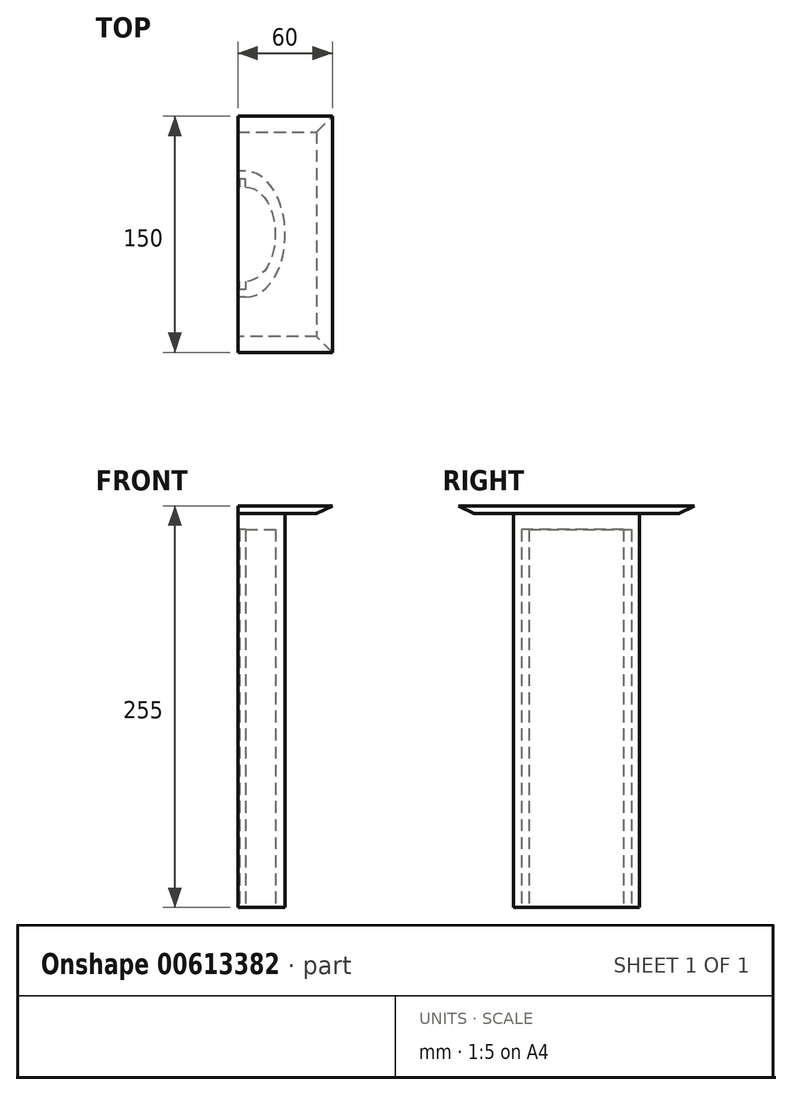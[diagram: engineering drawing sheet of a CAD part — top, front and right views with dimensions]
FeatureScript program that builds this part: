
annotation { "Feature Type Name" : "Feature", "Feature Type Description" : "" }
export const myFeature = defineFeature(function(context is Context, id is Id, definition is map)
    precondition{}
    {
        {
            var Q0;
            Q0=qCreatedBy(makeId("Top.planeOp"),FACE);
            var sketch = newSketch(context, id + "F0", { "sketchPlane" : qUnion([Q0])});
            skEllipticalArc(sketch, "E0", {});
            skPoint(sketch, "E1.oppositeSnap0", {"position": v(6, 33.86) * mm});
            skLineSegment(sketch, "E1.bottom", {"start": v(6, -46.14) * mm, "end": v(1, -46.14) * mm});
            skLineSegment(sketch, "E1.top", {"start": v(6, 33.86) * mm, "end": v(1, 33.86) * mm});
            skLineSegment(sketch, "E1.right", {"start": v(1, -46.14) * mm, "end": v(1, 33.86) * mm});
            const initialGuessF0  = {"E0": [0.006, -0.006144226491451254, 0, -1, 0.04, 0.025, 0, 3.141592653589793]};
            skSetInitialGuess(sketch, initialGuessF0);
            skSolve(sketch);
        }
        {
            var Q0;
            Q0=makeQuery(id+"F0.imprint","IMPRINT",FACE,{"disambiguationData":[TD([[makeQuery(id+"F0.imprint","IMPRINT",EDGE,{"derivedFrom":sQuery(id+"F0.wireOp",EDGE,"E0")}),1.0]])]});
            extrude(context, id + "F1", {"entities" : qUnion([Q0]), "depth" : 250 * mm, "offsetDistance" : 25 * mm});
        }
        {
            var Q0;
            Q0=makeQuery(id+"F1.opExtrude","CAP_FACE",FACE,{"disambiguationData":[OSD([sQuery(id+"F0.wireOp",EDGE,"E0"),sQuery(id+"F0.wireOp",EDGE,"E1.bottom"),sQuery(id+"F0.wireOp",EDGE,"E1.top"),sQuery(id+"F0.wireOp",EDGE,"E1.right")])],"isStart":false});
            var sketch = newSketch(context, id + "F2", { "sketchPlane" : qUnion([Q0])});
            skLineSegment(sketch, "E2.bottom", {"start": v(61, 68.86) * mm, "end": v(1, 68.86) * mm});
            skLineSegment(sketch, "E2.top", {"start": v(61, -81.14) * mm, "end": v(1, -81.14) * mm});
            skLineSegment(sketch, "E2.left", {"start": v(61, 68.86) * mm, "end": v(61, -81.14) * mm});
            skLineSegment(sketch, "E2.right", {"start": v(1, 68.86) * mm, "end": v(1, -81.14) * mm});
            skSolve(sketch);
        }
        {
            var Q0;
            {var subQ2=sQuery(id+"F2.wireOp",EDGE,"E2.bottom");Q0=makeQuery(id+"F2.imprint","IMPRINT",FACE,{"disambiguationData":[TD([[makeQuery(id+"F2.imprint","IMPRINT",EDGE,{"derivedFrom":subQ2}),1.0]])]});}
            var Q1;
            Q1=makeQuery(id+"F2.imprint","IMPRINT",FACE,{"disambiguationData":[TD([[makeQuery(id+"F2.imprint","IMPRINT",EDGE,{"derivedFrom":makeQuery(id+"F1.opExtrude","CAP_EDGE",EDGE,{"disambiguationData":[OSD([sQuery(id+"F0.wireOp",EDGE,"E0")])],"isStart":false})}),1.0]])]});
            extrude(context, id + "F3", {"entities" : qUnion([Q0, Q1]), "operationType" : NewBodyOperationType.ADD, "depth" : 5 * mm, "offsetDistance" : 25 * mm});
        }
        {
            var Q0;
            Q0=makeQuery(id+"F3.opExtrude","CAP_EDGE",EDGE,{"disambiguationData":[OSD([sQuery(id+"F2.wireOp",EDGE,"E2.bottom")])],"isStart":true});
            var Q1;
            Q1=makeQuery(id+"F3.opExtrude","CAP_EDGE",EDGE,{"disambiguationData":[OSD([sQuery(id+"F2.wireOp",EDGE,"E2.left")])],"isStart":true});
            var Q2;
            Q2=makeQuery(id+"F3.opExtrude","CAP_EDGE",EDGE,{"disambiguationData":[OSD([sQuery(id+"F2.wireOp",EDGE,"E2.top")])],"isStart":true});
            chamfer(context, id + "F4", {"entities" : qUnion([Q0, Q1, Q2]), "chamferType" : ChamferType.TWO_OFFSETS, "width1" : 5 * mm, "oppositeDirection" : false, "width2" : 10 * mm, "tangentPropagation" : true});
        }
        {
            var Q0;
            Q0=makeQuery(id+"F1.opExtrude","CAP_FACE",FACE,{"disambiguationData":[OSD([sQuery(id+"F0.wireOp",EDGE,"E0"),sQuery(id+"F0.wireOp",EDGE,"E1.bottom"),sQuery(id+"F0.wireOp",EDGE,"E1.top"),sQuery(id+"F0.wireOp",EDGE,"E1.right")])],"isStart":true});
            var sketch = newSketch(context, id + "F5", { "sketchPlane" : qUnion([Q0])});
            skEllipticalArc(sketch, "E3", {});
            skLineSegment(sketch, "E4", {"start": v(6, -23.86) * mm, "end": v(1, -23.86) * mm});
            skLineSegment(sketch, "E5", {"start": v(6, 36.14) * mm, "end": v(1, 36.14) * mm});
            skLineSegment(sketch, "E6", {"start": v(1, -23.86) * mm, "end": v(1, 36.14) * mm});
            skPoint(sketch, "E7.orphan", {"position": v(0, -23.86) * mm});
            skLineSegment(sketch, "E8.bottom", {"start": v(3.5, -23.86) * mm, "end": v(6, -23.86) * mm});
            skLineSegment(sketch, "E8.right", {"start": v(6, -23.86) * mm, "end": v(6, -28.86) * mm});
            skLineSegment(sketch, "E9", {"start": v(1, 6.14) * mm, "end": v(6, 6.14) * mm});
            skPoint(sketch, "E8.top.start.orphan", {"position": v(3.5, -28.86) * mm});
            skLineSegment(sketch, "E10", {"start": v(6, -28.86) * mm, "end": v(2, -28.86) * mm});
            skLineSegment(sketch, "E11", {"start": v(2, -28.86) * mm, "end": v(2, -23.86) * mm});
            skLineSegment(sketch, "E12", {"start": v(2, -23.86) * mm, "end": v(3.5, -23.86) * mm});
            skPoint(sketch, "E13.MirrorCS.end.orphan", {"position": v(3.5, 41.14) * mm});
            skPoint(sketch, "E13.MirrorCS.start.orphan", {"position": v(3.5, 36.14) * mm});
            skPoint(sketch, "E14.MirrorCS.end.orphan", {"position": v(6, 41.14) * mm});
            skPoint(sketch, "E15.MirrorCS.start.orphan", {"position": v(6, 36.14) * mm});
            skLineSegment(sketch, "E16.MirrorCS", {"start": v(6, 36.14) * mm, "end": v(6, 41.14) * mm});
            skLineSegment(sketch, "E17.MirrorCS", {"start": v(6, 41.14) * mm, "end": v(2, 41.14) * mm});
            skLineSegment(sketch, "E18.MirrorCS", {"start": v(2, 41.14) * mm, "end": v(2, 36.14) * mm});
            skLineSegment(sketch, "E19.MirrorCS", {"start": v(3.5, 36.14) * mm, "end": v(6, 36.14) * mm});
            skLineSegment(sketch, "E20.MirrorCS", {"start": v(2, 36.14) * mm, "end": v(3.5, 36.14) * mm});
            const initialGuessF5  = {"E3": [0.006, 0.006144226491451254, 0, -1, 0.03, 0.01875, 0, 3.141592653589793]};
            skSetInitialGuess(sketch, initialGuessF5);
            skSolve(sketch);
        }
        {
            var Q0;
            {var subQ6=sQuery(id+"F5.wireOp",EDGE,"E3");Q0=makeQuery(id+"F5.imprint","IMPRINT",FACE,{"disambiguationData":[TD([[makeQuery(id+"F5.imprint","IMPRINT",EDGE,{"derivedFrom":subQ6}),1.0]])]});}
            var Q1;
            Q1=makeQuery(id+"F5.imprint","IMPRINT",FACE,{"disambiguationData":[TD([[makeQuery(id+"F5.imprint","IMPRINT",EDGE,{"derivedFrom":sQuery(id+"F5.wireOp",EDGE,"E13.MirrorCS")}),-1.0]])]});
            var Q2;
            {var subQ0=sQuery(id+"F5.wireOp",EDGE,"E8.right");Q2=makeQuery(id+"F5.imprint","IMPRINT",FACE,{"disambiguationData":[TD([[makeQuery(id+"F5.imprint","IMPRINT",EDGE,{"derivedFrom":subQ0}),-1.0]])]});}
            var Q3;
            {var subQ0=sQuery(id+"F5.wireOp",EDGE,"E16.MirrorCS");Q3=makeQuery(id+"F5.imprint","IMPRINT",FACE,{"disambiguationData":[TD([[makeQuery(id+"F5.imprint","IMPRINT",EDGE,{"derivedFrom":subQ0}),1.0]])]});}
            extrude(context, id + "F6", {"entities" : qUnion([Q0, Q1, Q2, Q3]), "operationType" : NewBodyOperationType.REMOVE, "oppositeDirection" : true, "depth" : 240 * mm, "offsetDistance" : 25 * mm});
        }
    });
